# Revit family: Maxlogic siren,flaşör,flaşörlü siren (Yüksek ıp)
name_source: partatom
category: Fire Alarm Devices
units: mm (PartAtom-declared; Revit-internal decimal feet)

## family parameters
Cut with Voids When Loaded = No
Host = Face
Maintain Annotation Orientation = Yes
OmniClass Number = 23.85.30.21
OmniClass Title = Environmental Detection/Registration
Part Type = Normal
Room Calculation Point = No
Round Connector Dimension = Use Diameter
Shared = No

## types (18) — shared parameters
Color = Kırmızı
Fax Number = (+)90 216 466 45 10
Installation Manual = https://mavilielektronik.com
Main Material = Red Plastic PC/ABS
Manufacturer = Mavili Elektronik Ticaret A.Ş.
Model = Maxlogic
Mounting height = Zeminden 2,4 m yukarıda
Mounting surface = Duvara montaj
Nominal Height = 95 mm
Nominal Width = 95 mm
Operating temperature = (-25°C) - (+70°C)
Operatonal Voltage (default) = 24 V/DC
Secondary Material = Plastic
URL = https://www.mavili.com.tr
Warranty Duration Labor = 2
Warranty Duration Parts = 2
Warranty Duration Unit = Year
zero-valued in all types: Cost, Default Elevation

## per-type parameters (varying)
| type | Code Performance | Description | Device Adress Setup | Flaşör | Flaşör,flaşörlü siren Tavan | IP 33 Taban | IP 65 Taban | Nominal Depth | Operating voltage range | Product Code | Protection Sign | Siren Tavan | Weight |
| Maxlogic Konvansiyonel Siren, Hava Şartlarına Dayanıklı(IP33) | EN 54-3 | Konvansiyonel Siren |  | No | No | Yes | No | 82 mm | 21-28V/DC | ML-2440 | IP 33 | Yes | 154 |
| Maxlogic Konvansiyonel Flaşör, Hava Şartlarına Dayanıklı(IP33) | EN 54-23 | Konvansiyonel Flaşör |  | Yes | Yes | Yes | No | 82 mm | 21-28V/DC | ML-2450 | IP 33 | No | 149 gr |
| Maxlogic Konvansiyonel Flaşörlü Siren, Hava Şartlarına Dayanıklı(IP33) | EN 54-3 / EN 54-23 | Konvansiyonel Flaşörlü siren |  | Yes | Yes | Yes | No | 82 mm | 21-28V/DC | ML-2460 | IP 33 | No | 166 gr |
| Maxlogic Konvansiyonel Siren, Hava Şartlarına Dayanıklı(IP65) | EN 54-3 | Konvansiyonel Siren |  | No | No | No | Yes | 100 mm | 21-28V/DC | ML-2470 | IP 65 | Yes | 173 gr |
| Maxlogic Konvansiyonel Flaşör, Hava Şartlarına Dayanıklı(IP65) | EN 54-23 | Konvansiyonel Flaşör |  | Yes | Yes | No | Yes | 107 mm | 21-28V/DC | ML-2480 | IP 65 | No | 168 gr |
| Maxlogic Konvansiyonel Flaşörlü Siren, Hava Şartlarına Dayanıklı(IP65) | EN 54-3 / EN 54-23 | Konvansiyonel Flaşörlü siren |  | Yes | Yes | No | Yes | 107 mm | 21-28V/DC | ML-2490 | IP 65 | No | 185 gr |
| Maxlogic Akıllı Adresli Sistem Siren, Hava Şartlarına Dayanıklı (IP33) | EN 54-3 | Akıllı Adresli Sistem Siren | El tipi adresleme cihazı | No | No | Yes | No | 82 mm | 18-33V/DC | ML-1440 | IP 33 | Yes | 159 gr |
| Maxlogic Akıllı Adresli Sistem Siren, Hava Şartlarına Dayanıklı (IP33), Kısa Devre İzolatörlü | EN 54-3 | Akıllı Adresli Sistem Siren kısa devre izolatörlü | El tipi adresleme cihazı | No | No | Yes | No | 82 mm | 18-33V/DC | ML-1440.SCI | IP 33 | Yes | 159 gr |
| Maxlogic Akıllı Adresli Sistem Flaşör, Hava Şartlarına Dayanıklı (IP33) | EN 54-23 | Akıllı Adresli Sistem Flaşör | El tipi adresleme cihazı | Yes | Yes | Yes | No | 82 mm | 18-33V/DC | ML-1450 | IP 33 | No | 153 gr |
| Maxlogic Akıllı Adresli Sistem Flaşör, Hava Şartlarına Dayanıklı (IP33), Kısa Devre İzolatörlü | EN 54-23 | Akıllı Adresli Sistem Flaşör kısa devre izolatörlü | El tipi adresleme cihazı | Yes | Yes | Yes | No | 82 mm | 18-33V/DC | ML-1450.SCI | IP 33 | No | 153 gr |
| Maxlogic Akıllı Adresli Sistem Flaşörlü Siren, Hava Şartlarına Dayanıklı (IP33) | EN 54-3 / EN 54-23 | Akıllı Adresli Sistem Flaşörlü siren | El tipi adresleme cihazı | Yes | Yes | Yes | No | 82 mm | 18-33V/DC | ML-1460 | IP 33 | No | 169 gr |
| Maxlogic Akıllı Adresli Sistem Flaşörlü Siren, Hava Şartlarına Dayanıklı (IP33),Kısa Devre İzolatörlü | EN 54-3 / EN 54-23 | Akıllı Adresli Sistem Flaşörlü siren kısa devre izolatörlü | El tipi adresleme cihazı | Yes | Yes | Yes | No | 82 mm | 18-33V/DC | ML-1460.SCI | IP 33 | No | 169 gr |
| Maxlogic Akıllı Adresli Sistem Siren, Hava Şartlarına Dayanıklı (IP65) | EN 54-3 | Akıllı Adresli Sistem Siren | El tipi adresleme cihazı | No | No | No | Yes | 82 mm | 18-33V/DC | ML-1470 | IP 65 | Yes | 178 gr |
| Maxlogic Akıllı Adresli Sistem Siren, Hava Şartlarına Dayanıklı (IP65), Kısa Devre İzolatörlü | EN 54-3 | Akıllı Adresli Sistem Siren kısa devre izolatörlü | El tipi adresleme cihazı | No | No | No | Yes | 82 mm | 18-33V/DC | ML-1470.SCI | IP 65 | Yes | 178 gr |
| Maxlogic Akıllı Adresli Sistem Flaşör, Hava Şartlarına Dayanıklı (IP65) | EN 54-23 | Akıllı Adresli Sistem Flaşör | El tipi adresleme cihazı | Yes | Yes | No | Yes | 82 mm | 18-33V/DC | ML-1480 | IP 65 | No | 172 gr |
| Maxlogic Akıllı Adresli Sistem Flaşör, Hava Şartlarına Dayanıklı (IP65), Kısa Devre İzolatörlü | EN 54-23 | Akıllı Adresli Sistem Flaşör kısa devre izolatörlü | El tipi adresleme cihazı | Yes | Yes | No | Yes | 82 mm | 18-33V/DC | ML-1480.SCI | IP 65 | No | 172 gr |
| Maxlogic Akıllı Adresli Sistem Flaşörlü Siren, Hava Şartlarına Dayanıklı (IP65) | EN 54-3 / EN 54-23 | Akıllı Adresli Sistem Flaşörlü siren | El tipi adresleme cihazı | Yes | Yes | No | Yes | 82 mm | 18-33V/DC | ML-1490 | IP 65 | No | 188 gr |
| Maxlogic Akıllı Adresli Sistem Flaşörlü Siren, Hava Şartlarına Dayanıklı (IP65),Kısa Devre İzolatörlü | EN 54-3 / EN 54-23 | Akıllı Adresli Sistem Flaşörlü siren kısa devre izolatörlü | El tipi adresleme cihazı | Yes | Yes | No | Yes | 82 mm | 18-33V/DC | ML-1490.SCI | IP 65 | No | 188 gr |

## geometry (parser evidence)
native form markers: Sweep x5
no freeform markers — native parametric forms only
